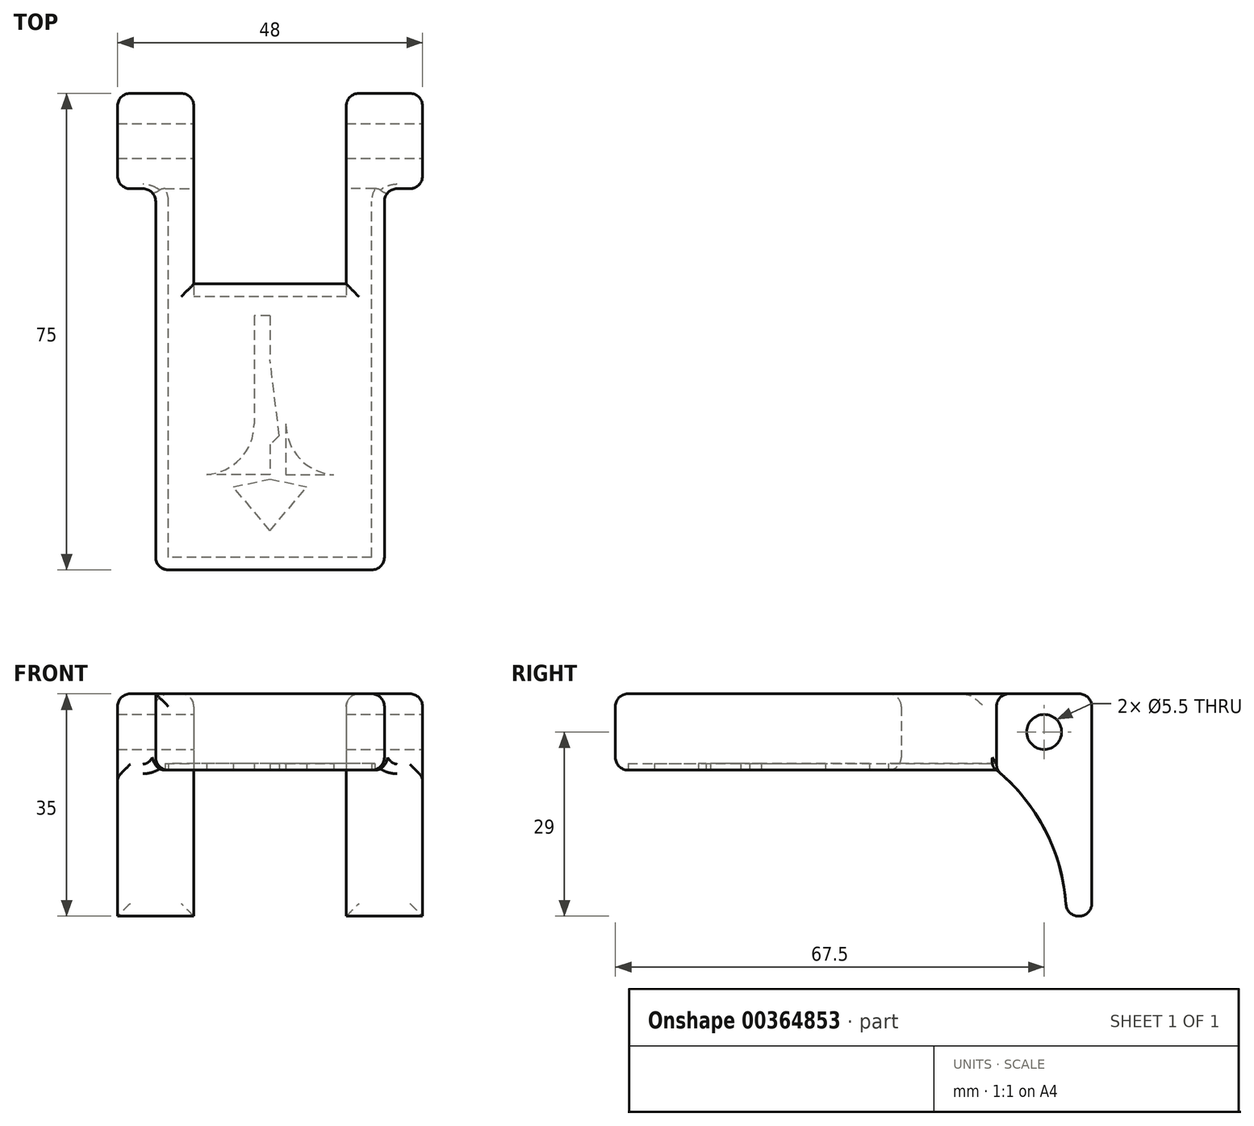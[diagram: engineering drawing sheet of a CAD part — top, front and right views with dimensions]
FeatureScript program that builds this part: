
annotation { "Feature Type Name" : "Feature", "Feature Type Description" : "" }
export const myFeature = defineFeature(function(context is Context, id is Id, definition is map)
    precondition{}
    {
        {
            var Q0;
            Q0=qCreatedBy(makeId("Front.planeOp"),FACE);
            var sketch = newSketch(context, id + "F0", { "sketchPlane" : qUnion([Q0])});
            skLineSegment(sketch, "E0.bottom", {"start": v(18, -6) * mm, "end": v(-18, -6) * mm});
            skLineSegment(sketch, "E0.top", {"start": v(18, 6) * mm, "end": v(-18, 6) * mm});
            skLineSegment(sketch, "E0.left", {"start": v(18, -6) * mm, "end": v(18, 6) * mm});
            skLineSegment(sketch, "E0.right", {"start": v(-18, -6) * mm, "end": v(-18, 6) * mm});
            skPoint(sketch, "E0.middle", {"position": v(0, 0) * mm});
            skSolve(sketch);
        }
        {
            var Q0;
            Q0 = qSketchRegion(id + "F0", true);
            extrude(context, id + "F1", {"entities" : qUnion([Q0]), "depth" : 45 * mm});
        }
        {
            var Q0;
            Q0=makeQuery(id+"F1.opExtrude","CAP_FACE",FACE,{"disambiguationData":[OSD([sQuery(id+"F0.wireOp",EDGE,"E0.bottom"),sQuery(id+"F0.wireOp",EDGE,"E0.top"),sQuery(id+"F0.wireOp",EDGE,"E0.left"),sQuery(id+"F0.wireOp",EDGE,"E0.right")])],"isStart":true});
            var sketch = newSketch(context, id + "F2", { "sketchPlane" : qUnion([Q0])});
            skLineSegment(sketch, "E1", {"start": v(0, 0) * mm, "end": v(-18, 0) * mm});
            skLineSegment(sketch, "E2", {"start": v(0, 0) * mm, "end": v(18, 0) * mm});
            skLineSegment(sketch, "E3", {"start": v(-18, 0) * mm, "end": v(-18, 6) * mm});
            skLineSegment(sketch, "E4", {"start": v(-18, 6) * mm, "end": v(-12, 6) * mm});
            skLineSegment(sketch, "E5", {"start": v(-12, 6) * mm, "end": v(-12, -6) * mm});
            skLineSegment(sketch, "E6", {"start": v(-12, -6) * mm, "end": v(-18, -6) * mm});
            skLineSegment(sketch, "E7", {"start": v(-18, -6) * mm, "end": v(-18, 0) * mm});
            skLineSegment(sketch, "E8", {"start": v(18, 0) * mm, "end": v(18, 6) * mm});
            skLineSegment(sketch, "E9", {"start": v(18, 6) * mm, "end": v(12, 6) * mm});
            skLineSegment(sketch, "E10", {"start": v(12, 6) * mm, "end": v(12, -6) * mm});
            skLineSegment(sketch, "E11", {"start": v(12, -6) * mm, "end": v(18, -6) * mm});
            skLineSegment(sketch, "E12", {"start": v(18, -6) * mm, "end": v(18, 0) * mm});
            skSolve(sketch);
        }
        {
            var Q0;
            {var subQ0=sQuery(id+"F2.wireOp",EDGE,"E3");Q0=makeQuery(id+"F2.imprint","IMPRINT",FACE,{"disambiguationData":[TD([[makeQuery(id+"F2.imprint","IMPRINT",EDGE,{"derivedFrom":subQ0}),-1.0]])]});}
            var Q1;
            {var subQ4=sQuery(id+"F2.wireOp",EDGE,"E6");Q1=makeQuery(id+"F2.imprint","IMPRINT",FACE,{"disambiguationData":[TD([[makeQuery(id+"F2.imprint","IMPRINT",EDGE,{"derivedFrom":subQ4}),1.0]])]});}
            var Q2;
            {var subQ4=sQuery(id+"F2.wireOp",EDGE,"E11");Q2=makeQuery(id+"F2.imprint","IMPRINT",FACE,{"disambiguationData":[TD([[makeQuery(id+"F2.imprint","IMPRINT",EDGE,{"derivedFrom":subQ4}),1.0]])]});}
            var Q3;
            {var subQ0=sQuery(id+"F2.wireOp",EDGE,"E8");Q3=makeQuery(id+"F2.imprint","IMPRINT",FACE,{"disambiguationData":[TD([[makeQuery(id+"F2.imprint","IMPRINT",EDGE,{"derivedFrom":subQ0}),1.0]])]});}
            extrude(context, id + "F3", {"entities" : qUnion([Q0, Q1, Q2, Q3]), "operationType" : NewBodyOperationType.ADD, "depth" : 30 * mm});
        }
        {
            var Q0;
            Q0=makeQuery(id+"F3.boolean.opBoolean","MERGE",FACE,{"derivedFrom":[makeQuery(id+"F1.opExtrude","SWEPT_FACE",FACE,{"disambiguationData":[OSD([sQuery(id+"F0.wireOp",EDGE,"E0.left")])]}),makeQuery(id+"F3.opExtrude","SWEPT_FACE",FACE,{"disambiguationData":[OSD([sQuery(id+"F2.wireOp",EDGE,"E3"),sQuery(id+"F2.wireOp",EDGE,"E7")])]})]});
            var sketch = newSketch(context, id + "F4", { "sketchPlane" : qUnion([Q0])});
            skLineSegment(sketch, "E13", {"start": v(30, 6) * mm, "end": v(30, -29) * mm});
            skLineSegment(sketch, "E14", {"start": v(30, -29) * mm, "end": v(26, -29) * mm});
            skLineSegment(sketch, "E15", {"start": v(30, 6) * mm, "end": v(15, 6) * mm});
            skLineSegment(sketch, "E16", {"start": v(15, 6) * mm, "end": v(15, -6) * mm});
            skArc(sketch, "E17", {"start": v(26, -29) * mm, "mid": v(23.06, -16.27) * mm, "end": v(15, -6) * mm});
            skSolve(sketch);
        }
        {
            var Q0;
            Q0 = qSketchRegion(id + "F4", true);
            extrude(context, id + "F5", {"entities" : qUnion([Q0]), "operationType" : NewBodyOperationType.ADD, "endBound" : BoundingType.SYMMETRIC, "depth" : 12 * mm});
        }
        {
            var Q0;
            Q0=makeQuery(id+"F3.boolean.opBoolean","MERGE",FACE,{"derivedFrom":[makeQuery(id+"F1.opExtrude","SWEPT_FACE",FACE,{"disambiguationData":[OSD([sQuery(id+"F0.wireOp",EDGE,"E0.right")])]}),makeQuery(id+"F3.opExtrude","SWEPT_FACE",FACE,{"disambiguationData":[OSD([sQuery(id+"F2.wireOp",EDGE,"E8"),sQuery(id+"F2.wireOp",EDGE,"E12")])]})]});
            var sketch = newSketch(context, id + "F6", { "sketchPlane" : qUnion([Q0])});
            skLineSegment(sketch, "E18", {"start": v(-30, 6) * mm, "end": v(-30, -29) * mm});
            skLineSegment(sketch, "E19", {"start": v(-30, -29) * mm, "end": v(-26, -29) * mm});
            skLineSegment(sketch, "E20", {"start": v(-30, 6) * mm, "end": v(-15, 6) * mm});
            skLineSegment(sketch, "E21", {"start": v(-15, 6) * mm, "end": v(-15, -6) * mm});
            skLineSegment(sketch, "E22", {"start": v(-15, -6) * mm, "end": v(-30, -6) * mm});
            skArc(sketch, "E23", {"start": v(-15, -6) * mm, "mid": v(-23.06, -16.27) * mm, "end": v(-26, -29) * mm});
            skSolve(sketch);
        }
        {
            var Q0;
            {var subQ2=sQuery(id+"F6.wireOp",EDGE,"E20");Q0=makeQuery(id+"F6.imprint","IMPRINT",FACE,{"disambiguationData":[TD([[makeQuery(id+"F6.imprint","IMPRINT",EDGE,{"derivedFrom":subQ2}),1.0]])]});}
            var Q1;
            {var subQ2=sQuery(id+"F6.wireOp",EDGE,"E19");Q1=makeQuery(id+"F6.imprint","IMPRINT",FACE,{"disambiguationData":[TD([[makeQuery(id+"F6.imprint","IMPRINT",EDGE,{"derivedFrom":subQ2}),1.0]])]});}
            extrude(context, id + "F7", {"entities" : qUnion([Q0, Q1]), "operationType" : NewBodyOperationType.ADD, "endBound" : BoundingType.SYMMETRIC, "depth" : 12 * mm});
        }
        {
            var Q0;
            Q0=makeQuery(id+"F3.boolean.opBoolean","MERGE",EDGE,{"derivedFrom":[makeQuery(id+"F1.opExtrude","SWEPT_EDGE",EDGE,{"disambiguationData":[OSD([sQuery(id+"F0.wireOp",EDGE,"E0.top"),sQuery(id+"F0.wireOp",EDGE,"E0.left")])]}),makeQuery(id+"F3.opExtrude","SWEPT_EDGE",EDGE,{"disambiguationData":[OSD([sQuery(id+"F2.wireOp",EDGE,"E3"),sQuery(id+"F2.wireOp",EDGE,"E4")])]})]});
            var Q1;
            Q1=makeQuery(id+"F1.opExtrude","CAP_EDGE",EDGE,{"disambiguationData":[OSD([sQuery(id+"F0.wireOp",EDGE,"E0.top")])],"isStart":false});
            var Q2;
            Q2=makeQuery(id+"F3.boolean.opBoolean","MERGE",EDGE,{"derivedFrom":[makeQuery(id+"F1.opExtrude","SWEPT_EDGE",EDGE,{"disambiguationData":[OSD([sQuery(id+"F0.wireOp",EDGE,"E0.bottom"),sQuery(id+"F0.wireOp",EDGE,"E0.left")])]}),makeQuery(id+"F3.opExtrude","SWEPT_EDGE",EDGE,{"disambiguationData":[OSD([sQuery(id+"F2.wireOp",EDGE,"E6"),sQuery(id+"F2.wireOp",EDGE,"E7")])]})]});
            var Q3;
            Q3=makeQuery(id+"F1.opExtrude","CAP_EDGE",EDGE,{"disambiguationData":[OSD([sQuery(id+"F0.wireOp",EDGE,"E0.left")])],"isStart":false});
            var Q4;
            Q4=makeQuery(id+"F1.opExtrude","CAP_EDGE",EDGE,{"disambiguationData":[OSD([sQuery(id+"F0.wireOp",EDGE,"E0.right")])],"isStart":false});
            var Q5;
            Q5=makeQuery(id+"F1.opExtrude","CAP_EDGE",EDGE,{"disambiguationData":[OSD([sQuery(id+"F0.wireOp",EDGE,"E0.bottom")])],"isStart":false});
            var Q6;
            Q6=makeQuery(id+"F1.opExtrude","CAP_EDGE",EDGE,{"disambiguationData":[OSD([sQuery(id+"F0.wireOp",EDGE,"E0.top")])],"isStart":true});
            var Q7;
            Q7=makeQuery(id+"F3.opExtrude","SWEPT_EDGE",EDGE,{"disambiguationData":[OSD([sQuery(id+"F0.wireOp",EDGE,"E0.top"),sQuery(id+"F2.wireOp",EDGE,"E9"),sQuery(id+"F2.wireOp",EDGE,"E10")])]});
            var Q8;
            Q8=makeQuery(id+"F7.boolean.opBoolean","MERGE",EDGE,{"derivedFrom":[makeQuery(id+"F3.opExtrude","CAP_EDGE",EDGE,{"disambiguationData":[OSD([sQuery(id+"F2.wireOp",EDGE,"E9")])],"isStart":false}),makeQuery(id+"F7.opExtrude","SWEPT_EDGE",EDGE,{"disambiguationData":[OSD([sQuery(id+"F6.wireOp",EDGE,"E18"),sQuery(id+"F6.wireOp",EDGE,"E20")])]})]});
            var Q9;
            Q9=makeQuery(id+"F3.opExtrude","SWEPT_EDGE",EDGE,{"disambiguationData":[OSD([sQuery(id+"F0.wireOp",EDGE,"E0.top"),sQuery(id+"F2.wireOp",EDGE,"E4"),sQuery(id+"F2.wireOp",EDGE,"E5")])]});
            var Q10;
            Q10=makeQuery(id+"F5.boolean.opBoolean","MERGE",EDGE,{"derivedFrom":[makeQuery(id+"F3.opExtrude","CAP_EDGE",EDGE,{"disambiguationData":[OSD([sQuery(id+"F2.wireOp",EDGE,"E4")])],"isStart":false}),makeQuery(id+"F5.opExtrude","SWEPT_EDGE",EDGE,{"disambiguationData":[OSD([sQuery(id+"F4.wireOp",EDGE,"E13"),sQuery(id+"F4.wireOp",EDGE,"E15")])]})]});
            var Q11;
            Q11=makeQuery(id+"F5.opExtrude","CAP_EDGE",EDGE,{"disambiguationData":[OSD([sQuery(id+"F4.wireOp",EDGE,"E15")])],"isStart":false});
            var Q12;
            Q12=makeQuery(id+"F5.opExtrude","SWEPT_EDGE",EDGE,{"disambiguationData":[OSD([sQuery(id+"F0.wireOp",EDGE,"E0.top"),sQuery(id+"F0.wireOp",EDGE,"E0.left"),sQuery(id+"F2.wireOp",EDGE,"E3"),sQuery(id+"F2.wireOp",EDGE,"E4"),sQuery(id+"F4.wireOp",EDGE,"E15"),sQuery(id+"F4.wireOp",EDGE,"E16")])]});
            var Q13;
            Q13=makeQuery(id+"F7.opExtrude","SWEPT_EDGE",EDGE,{"disambiguationData":[OSD([sQuery(id+"F0.wireOp",EDGE,"E0.top"),sQuery(id+"F0.wireOp",EDGE,"E0.right"),sQuery(id+"F2.wireOp",EDGE,"E8"),sQuery(id+"F2.wireOp",EDGE,"E9"),sQuery(id+"F6.wireOp",EDGE,"E20"),sQuery(id+"F6.wireOp",EDGE,"E21")])]});
            var Q14;
            Q14=makeQuery(id+"F7.opExtrude","CAP_EDGE",EDGE,{"disambiguationData":[OSD([sQuery(id+"F6.wireOp",EDGE,"E20")])],"isStart":false});
            var Q15;
            Q15=makeQuery(id+"F3.boolean.opBoolean","MERGE",EDGE,{"derivedFrom":[makeQuery(id+"F1.opExtrude","SWEPT_EDGE",EDGE,{"disambiguationData":[OSD([sQuery(id+"F0.wireOp",EDGE,"E0.bottom"),sQuery(id+"F0.wireOp",EDGE,"E0.right")])]}),makeQuery(id+"F3.opExtrude","SWEPT_EDGE",EDGE,{"disambiguationData":[OSD([sQuery(id+"F2.wireOp",EDGE,"E11"),sQuery(id+"F2.wireOp",EDGE,"E12")])]})]});
            var Q16;
            Q16=makeQuery(id+"F7.opExtrude","CAP_EDGE",EDGE,{"disambiguationData":[OSD([sQuery(id+"F6.wireOp",EDGE,"E21")])],"isStart":false});
            var Q17;
            {var subQ0=sQuery(id+"F6.wireOp",EDGE,"E21");var subQ1=sQuery(id+"F6.wireOp",EDGE,"E23");Q17=makeQuery(id+"F7.boolean.opBoolean","SPLIT",EDGE,{"disambiguationData":[topologyDisambiguationEdgeConnected([makeQuery(id+"F7.opExtrude","SWEPT_FACE",FACE,{"disambiguationData":[OSD([subQ0])]})])],"derivedFrom":makeQuery(id+"F7.opExtrude","SWEPT_EDGE",EDGE,{"disambiguationData":[OSD([sQuery(id+"F0.wireOp",EDGE,"E0.bottom"),sQuery(id+"F0.wireOp",EDGE,"E0.right"),sQuery(id+"F2.wireOp",EDGE,"E11"),sQuery(id+"F2.wireOp",EDGE,"E12"),subQ0,sQuery(id+"F6.wireOp",EDGE,"E22"),subQ1])]})});}
            var Q18;
            Q18=makeQuery(id+"F7.boolean.opBoolean","INTERSECT",EDGE,{"derivedFrom":[makeQuery(id+"F3.boolean.opBoolean","MERGE",FACE,{"derivedFrom":[makeQuery(id+"F1.opExtrude","SWEPT_FACE",FACE,{"disambiguationData":[OSD([sQuery(id+"F0.wireOp",EDGE,"E0.right")])]}),makeQuery(id+"F3.opExtrude","SWEPT_FACE",FACE,{"disambiguationData":[OSD([sQuery(id+"F2.wireOp",EDGE,"E8"),sQuery(id+"F2.wireOp",EDGE,"E12")])]})]}),makeQuery(id+"F7.opExtrude","SWEPT_FACE",FACE,{"disambiguationData":[OSD([sQuery(id+"F6.wireOp",EDGE,"E21")])]})]});
            var Q19;
            Q19=makeQuery(id+"F5.boolean.opBoolean","INTERSECT",EDGE,{"derivedFrom":[makeQuery(id+"F3.boolean.opBoolean","MERGE",FACE,{"derivedFrom":[makeQuery(id+"F1.opExtrude","SWEPT_FACE",FACE,{"disambiguationData":[OSD([sQuery(id+"F0.wireOp",EDGE,"E0.left")])]}),makeQuery(id+"F3.opExtrude","SWEPT_FACE",FACE,{"disambiguationData":[OSD([sQuery(id+"F2.wireOp",EDGE,"E3"),sQuery(id+"F2.wireOp",EDGE,"E7")])]})]}),makeQuery(id+"F5.opExtrude","SWEPT_FACE",FACE,{"disambiguationData":[OSD([sQuery(id+"F4.wireOp",EDGE,"E16")])]})]});
            var Q20;
            {var subQ0=sQuery(id+"F4.wireOp",EDGE,"E16");var subQ1=sQuery(id+"F4.wireOp",EDGE,"E17");Q20=makeQuery(id+"F5.boolean.opBoolean","SPLIT",EDGE,{"disambiguationData":[topologyDisambiguationEdgeConnected([makeQuery(id+"F5.opExtrude","SWEPT_FACE",FACE,{"disambiguationData":[OSD([subQ0])]})])],"derivedFrom":makeQuery(id+"F5.opExtrude","SWEPT_EDGE",EDGE,{"disambiguationData":[OSD([sQuery(id+"F0.wireOp",EDGE,"E0.bottom"),sQuery(id+"F0.wireOp",EDGE,"E0.left"),sQuery(id+"F2.wireOp",EDGE,"E6"),sQuery(id+"F2.wireOp",EDGE,"E7"),subQ0,subQ1])]})});}
            var Q21;
            Q21=makeQuery(id+"F5.opExtrude","CAP_EDGE",EDGE,{"disambiguationData":[OSD([sQuery(id+"F4.wireOp",EDGE,"E16")])],"isStart":false});
            var Q22;
            Q22=makeQuery(id+"F5.opExtrude","CAP_EDGE",EDGE,{"disambiguationData":[OSD([sQuery(id+"F4.wireOp",EDGE,"E13")])],"isStart":false});
            var Q23;
            Q23=makeQuery(id+"F7.opExtrude","CAP_EDGE",EDGE,{"disambiguationData":[OSD([sQuery(id+"F6.wireOp",EDGE,"E18")])],"isStart":false});
            var Q24;
            Q24=makeQuery(id+"F7.boolean.opBoolean","MERGE",EDGE,{"derivedFrom":[makeQuery(id+"F3.opExtrude","CAP_EDGE",EDGE,{"disambiguationData":[OSD([sQuery(id+"F2.wireOp",EDGE,"E10")])],"isStart":false}),makeQuery(id+"F7.opExtrude","CAP_EDGE",EDGE,{"disambiguationData":[OSD([sQuery(id+"F6.wireOp",EDGE,"E18")])],"isStart":true})]});
            var Q25;
            Q25=makeQuery(id+"F5.boolean.opBoolean","MERGE",EDGE,{"derivedFrom":[makeQuery(id+"F3.opExtrude","CAP_EDGE",EDGE,{"disambiguationData":[OSD([sQuery(id+"F2.wireOp",EDGE,"E5")])],"isStart":false}),makeQuery(id+"F5.opExtrude","CAP_EDGE",EDGE,{"disambiguationData":[OSD([sQuery(id+"F4.wireOp",EDGE,"E13")])],"isStart":true})]});
            var Q26;
            Q26=makeQuery(id+"F3.opExtrude","CAP_EDGE",EDGE,{"disambiguationData":[OSD([sQuery(id+"F2.wireOp",EDGE,"E5")])],"isStart":true});
            var Q27;
            Q27=makeQuery(id+"F3.opExtrude","CAP_EDGE",EDGE,{"disambiguationData":[OSD([sQuery(id+"F2.wireOp",EDGE,"E10")])],"isStart":true});
            var Q28;
            Q28=makeQuery(id+"F1.opExtrude","CAP_EDGE",EDGE,{"disambiguationData":[OSD([sQuery(id+"F0.wireOp",EDGE,"E0.bottom")])],"isStart":true});
            var Q29;
            Q29=makeQuery(id+"F5.opExtrude","SWEPT_EDGE",EDGE,{"disambiguationData":[OSD([sQuery(id+"F4.wireOp",EDGE,"E13"),sQuery(id+"F4.wireOp",EDGE,"E14")])]});
            var Q30;
            Q30=makeQuery(id+"F7.opExtrude","SWEPT_EDGE",EDGE,{"disambiguationData":[OSD([sQuery(id+"F6.wireOp",EDGE,"E18"),sQuery(id+"F6.wireOp",EDGE,"E19")])]});
            var Q31;
            Q31=makeQuery(id+"F7.opExtrude","SWEPT_EDGE",EDGE,{"disambiguationData":[OSD([sQuery(id+"F6.wireOp",EDGE,"E19"),sQuery(id+"F6.wireOp",EDGE,"E23")])]});
            var Q32;
            Q32=makeQuery(id+"F5.opExtrude","SWEPT_EDGE",EDGE,{"disambiguationData":[OSD([sQuery(id+"F4.wireOp",EDGE,"E14"),sQuery(id+"F4.wireOp",EDGE,"E17")])]});
            fillet(context, id + "F8", {"entities" : qUnion([Q0, Q1, Q2, Q3, Q4, Q5, Q6, Q7, Q8, Q9, Q10, Q11, Q12, Q13, Q14, Q15, Q16, Q17, Q18, Q19, Q20, Q21, Q22, Q23, Q24, Q25, Q26, Q27, Q28, Q29, Q30, Q31, Q32]), "radius" : 2 * mm, "tangentPropagation" : true, "allowEdgeOverflow" : false});
        }
        {
            var Q0;
            Q0=makeQuery(id+"F5.opExtrude","CAP_FACE",FACE,{"disambiguationData":[OSD([sQuery(id+"F4.wireOp",EDGE,"E13"),sQuery(id+"F4.wireOp",EDGE,"E14"),sQuery(id+"F4.wireOp",EDGE,"E15"),sQuery(id+"F4.wireOp",EDGE,"E16"),sQuery(id+"F4.wireOp",EDGE,"E17")])],"isStart":false});
            var sketch = newSketch(context, id + "F9", { "sketchPlane" : qUnion([Q0])});
            skLineSegment(sketch, "E24", {"start": v(22.5, 4) * mm, "end": v(22.5, 0) * mm});
            skCircle(sketch, "E25", {"center": v(22.5, 0) * mm, "radius": 2.75 * mm});
            skSolve(sketch);
        }
        {
            var Q0;
            Q0=makeQuery(id+"F9.imprint","IMPRINT",FACE,{"disambiguationData":[TD([[makeQuery(id+"F9.imprint","IMPRINT",EDGE,{"derivedFrom":sQuery(id+"F9.wireOp",EDGE,"E25")}),1.0]])]});
            extrude(context, id + "F10", {"entities" : qUnion([Q0]), "operationType" : NewBodyOperationType.REMOVE, "oppositeDirection" : true, "depth" : 50 * mm});
        }
        {
            var Q0;
            Q0=makeQuery(id+"F3.boolean.opBoolean","MERGE",FACE,{"derivedFrom":[makeQuery(id+"F1.opExtrude","SWEPT_FACE",FACE,{"disambiguationData":[OSD([sQuery(id+"F0.wireOp",EDGE,"E0.bottom")])]}),makeQuery(id+"F3.opExtrude","SWEPT_FACE",FACE,{"disambiguationData":[OSD([sQuery(id+"F2.wireOp",EDGE,"E6")])]}),makeQuery(id+"F3.opExtrude","SWEPT_FACE",FACE,{"disambiguationData":[OSD([sQuery(id+"F2.wireOp",EDGE,"E11")])]})]});
            var sketch = newSketch(context, id + "F11", { "sketchPlane" : qUnion([Q0])});
            skLineSegment(sketch, "E26", {"start": v(0, 0) * mm, "end": v(0, 5) * mm});
            skLineSegment(sketch, "E27", {"start": v(0, 5) * mm, "end": v(-5, 5) * mm});
            skLineSegment(sketch, "E28", {"start": v(0, 5) * mm, "end": v(0, 30) * mm});
            skLineSegment(sketch, "E29", {"start": v(0, 30) * mm, "end": v(-10, 30) * mm});
            skLineSegment(sketch, "E30", {"start": v(0, 30) * mm, "end": v(0, 42) * mm});
            skLineSegment(sketch, "E31", {"start": v(-10, 30) * mm, "end": v(0, 42) * mm});
            skLineSegment(sketch, "E32", {"start": v(-2.5, 5) * mm, "end": v(-2.5, 30) * mm});
            skLineSegment(sketch, "E33", {"start": v(-2.5, 30) * mm, "end": v(-2.5, 22) * mm});
            skArc(sketch, "E34", {"start": v(-2.5, 22) * mm, "mid": v(-4.67, 27.48) * mm, "end": v(-10, 30) * mm});
            skLineSegment(sketch, "E35", {"start": v(0, 38.85) * mm, "end": v(-5.76, 31.94) * mm});
            skLineSegment(sketch, "E36", {"start": v(-5.76, 31.94) * mm, "end": v(0, 31.94) * mm});
            skLineSegment(sketch, "E37", {"start": v(-1.46, 23.87) * mm, "end": v(0, 25.27) * mm});
            skLineSegment(sketch, "E38", {"start": v(-1.46, 23.87) * mm, "end": v(0, 11.93) * mm});
            skLineSegment(sketch, "E39.MirrorCS", {"start": v(1.46, 23.87) * mm, "end": v(0, 25.27) * mm});
            skLineSegment(sketch, "E40.MirrorCS", {"start": v(1.46, 23.87) * mm, "end": v(0, 11.93) * mm});
            skLineSegment(sketch, "E41.MirrorCS", {"start": v(2.5, 5) * mm, "end": v(2.5, 30) * mm});
            skArc(sketch, "E42.MirrorCS", {"start": v(2.5, 22) * mm, "mid": v(4.67, 27.48) * mm, "end": v(10, 30) * mm});
            skLineSegment(sketch, "E43.MirrorCS", {"start": v(0, 5) * mm, "end": v(5, 5) * mm});
            skLineSegment(sketch, "E44.MirrorCS", {"start": v(10, 30) * mm, "end": v(0, 42) * mm});
            skLineSegment(sketch, "E45.MirrorCS", {"start": v(0, 38.85) * mm, "end": v(5.76, 31.94) * mm});
            skLineSegment(sketch, "E46.MirrorCS", {"start": v(5.76, 31.94) * mm, "end": v(0, 31.94) * mm});
            skLineSegment(sketch, "E47.MirrorCS", {"start": v(0, 30) * mm, "end": v(10, 30) * mm});
            skArc(sketch, "E48", {"start": v(-5, 5) * mm, "mid": v(-3.45, 5.5) * mm, "end": v(-2.5, 6.83) * mm});
            skArc(sketch, "E49", {"start": v(2.5, 6.83) * mm, "mid": v(3.45, 5.5) * mm, "end": v(5, 5) * mm});
            skLineSegment(sketch, "E50", {"start": v(-5.76, 31.94) * mm, "end": v(0, 30.7) * mm});
            skLineSegment(sketch, "E51", {"start": v(0, 30.7) * mm, "end": v(5.76, 31.94) * mm});
            skSolve(sketch);
        }
        {
            var Q0;
            {var subQ0=sQuery(id+"F11.wireOp",EDGE,"E31");Q0=makeQuery(id+"F11.imprint","IMPRINT",FACE,{"disambiguationData":[TD([[makeQuery(id+"F11.imprint","IMPRINT",EDGE,{"derivedFrom":subQ0}),-1.0]])]});}
            var Q1;
            {var subQ1=sQuery(id+"F11.wireOp",EDGE,"E44.MirrorCS");Q1=makeQuery(id+"F11.imprint","IMPRINT",FACE,{"disambiguationData":[TD([[makeQuery(id+"F11.imprint","IMPRINT",EDGE,{"derivedFrom":subQ1}),1.0]])]});}
            var Q2;
            {var subQ2=sQuery(id+"F11.wireOp",EDGE,"E33");Q2=makeQuery(id+"F11.imprint","IMPRINT",FACE,{"disambiguationData":[TD([[makeQuery(id+"F11.imprint","IMPRINT",EDGE,{"derivedFrom":subQ2}),-1.0]])]});}
            var Q3;
            {var subQ3=sQuery(id+"F11.wireOp",EDGE,"E42.MirrorCS");Q3=makeQuery(id+"F11.imprint","IMPRINT",FACE,{"disambiguationData":[TD([[makeQuery(id+"F11.imprint","IMPRINT",EDGE,{"derivedFrom":subQ3}),1.0]])]});}
            var Q4;
            {var subQ1=sQuery(id+"F11.wireOp",EDGE,"E39.MirrorCS");Q4=makeQuery(id+"F11.imprint","IMPRINT",FACE,{"disambiguationData":[TD([[makeQuery(id+"F11.imprint","IMPRINT",EDGE,{"derivedFrom":subQ1}),-1.0]])]});}
            var Q5;
            {var subQ7=sQuery(id+"F11.wireOp",EDGE,"E33");Q5=makeQuery(id+"F11.imprint","IMPRINT",FACE,{"disambiguationData":[TD([[makeQuery(id+"F11.imprint","IMPRINT",EDGE,{"derivedFrom":subQ7}),1.0]])]});}
            var Q6;
            {var subQ0=sQuery(id+"F11.wireOp",EDGE,"E48");Q6=makeQuery(id+"F11.imprint","IMPRINT",FACE,{"disambiguationData":[TD([[makeQuery(id+"F11.imprint","IMPRINT",EDGE,{"derivedFrom":subQ0}),-1.0]])]});}
            var Q7;
            {var subQ3=sQuery(id+"F11.wireOp",EDGE,"E49");Q7=makeQuery(id+"F11.imprint","IMPRINT",FACE,{"disambiguationData":[TD([[makeQuery(id+"F11.imprint","IMPRINT",EDGE,{"derivedFrom":subQ3}),-1.0]])]});}
            extrude(context, id + "F12", {"entities" : qUnion([Q0, Q1, Q2, Q3, Q4, Q5, Q6, Q7]), "operationType" : NewBodyOperationType.REMOVE, "oppositeDirection" : true, "depth" : 1 * mm});
        }
    });
